AUTODESK INVENTOR PART (.ipt)
format: ipt  version: 2011 SP1 (Build 150282100, 282)  size: 154,624 bytes
history: native  units: mm (DEFAULTED — no unit token found)
features: other x18, plane x3, sketch x3, sweep x3
ambient origin geometry x8: Origin, YZ Plane, XZ Plane, XY Plane, X Axis, Y Axis, Z Axis, Center Point
feature tree (27):
  other  "Work Point1"
  other  "Work Point2"
  other  "Segment1"
  plane  "Work Plane1"
  other  "Work Point5"
  other  "Work Point6"
  other  "Power:1"
  other  "Work Point7"
  other  "Work Point8"
  other  "Power:2"
  other  "Work Point9"
  other  "Segment2"
  other  "Work Point10"
  other  "Segment3"
  other  "Work Point11"
  other  "Work Point12"
  plane  "Work Plane3"
  plane  "Work Plane4"
  sketch  "Sketch1"  dims[d0=0.0mm d2=0.0mm]
  other  "Srf1"
  sketch  "Sketch3"  dims[d3=0.0mm]
  other  "Srf3"
  sketch  "Sketch4"
  other  "Srf4"
  sweep  "SweepSrf1"
  sweep  "SweepSrf3"
  sweep  "SweepSrf4"
